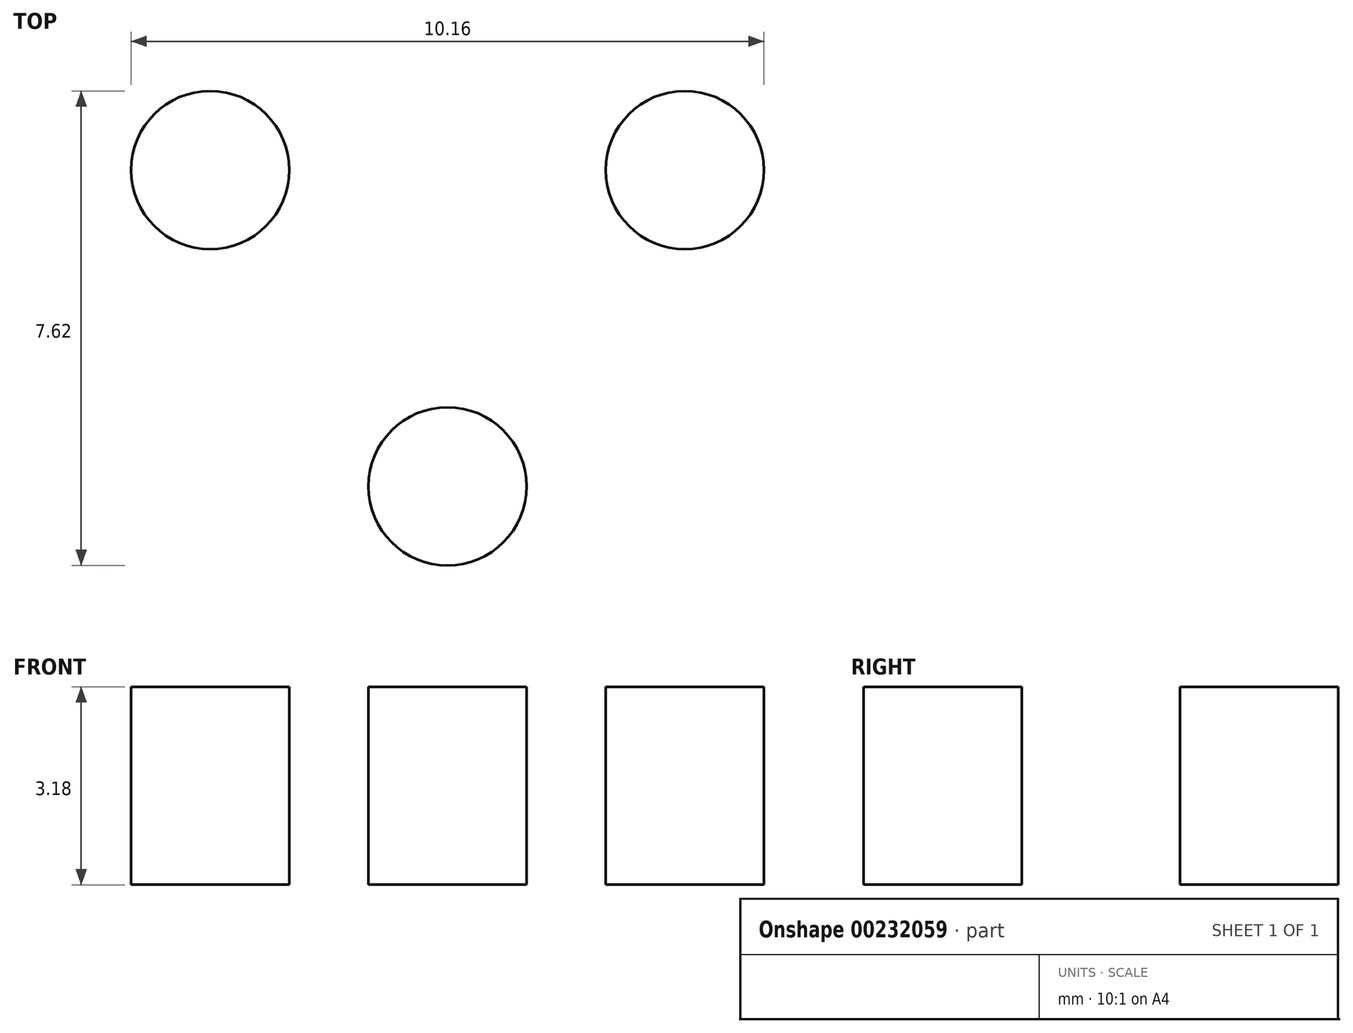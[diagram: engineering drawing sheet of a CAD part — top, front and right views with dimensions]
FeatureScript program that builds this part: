
annotation { "Feature Type Name" : "Feature", "Feature Type Description" : "" }
export const myFeature = defineFeature(function(context is Context, id is Id, definition is map)
    precondition{}
    {
        {
            var Q0;
            Q0=qCreatedBy(makeId("Top.planeOp"),FACE);
            var sketch = newSketch(context, id + "F0", { "sketchPlane" : qUnion([Q0])});
            skArc(sketch, "E0", {"start": v(0, 8.13) * mm, "mid": v(-8.13, 0) * mm, "end": v(0, -8.13) * mm});
            skLineSegment(sketch, "E1", {"start": v(0, 8.13) * mm, "end": v(20.32, 8.13) * mm});
            skLineSegment(sketch, "E2", {"start": v(0, -8.13) * mm, "end": v(18.29, -8.13) * mm});
            skArc(sketch, "E3", {"start": v(23.26, -9.18) * mm, "mid": v(18.82, -3.08) * mm, "end": v(13.2, -8.13) * mm});
            skLineSegment(sketch, "E4", {"start": v(20.32, 8.13) * mm, "end": v(37.22, -8.77) * mm});
            skLineSegment(sketch, "E5.0", {"start": v(23.26, -9.18) * mm, "end": v(31.82, -17.74) * mm});
            skPoint(sketch, "E6.centerSnap0", {"position": v(18.82, -3.08) * mm});
            skPoint(sketch, "E7.center.orphan", {"position": v(18.29, 8.13) * mm});
            skPoint(sketch, "E8.center.orphan", {"position": v(18.29, 0) * mm});
            skPoint(sketch, "E6.center.orphan", {"position": v(17.76, -3.08) * mm});
            skPoint(sketch, "E9.center.orphan", {"position": v(18.29, 2.23) * mm});
            skArc(sketch, "E10", {"start": v(31.82, -17.74) * mm, "mid": v(34.9, -13.49) * mm, "end": v(37.22, -8.77) * mm});
            skPoint(sketch, "E11.center.orphan", {"position": v(13.7, 2.23) * mm});
            skSolve(sketch);
        }
        {
            var Q0;
            {var subQ2=sQuery(id+"F0.wireOp",EDGE,"E0");Q0=makeQuery(id+"F0.imprint","IMPRINT",FACE,{"disambiguationData":[TD([[makeQuery(id+"F0.imprint","IMPRINT",EDGE,{"derivedFrom":subQ2}),1.0]])]});}
            extrude(context, id + "F1", {"entities" : qUnion([Q0]), "endBound" : BoundingType.SYMMETRIC, "depth" : 3.17 * mm});
        }
        {
            var Q0;
            Q0=makeQuery(id+"F1.opExtrude","CAP_FACE",FACE,{"disambiguationData":[OSD([sQuery(id+"F0.wireOp",EDGE,"E0"),sQuery(id+"F0.wireOp",EDGE,"E1"),sQuery(id+"F0.wireOp",EDGE,"E2"),sQuery(id+"F0.wireOp",EDGE,"E3"),sQuery(id+"F0.wireOp",EDGE,"E4"),sQuery(id+"F0.wireOp",EDGE,"E5.0"),sQuery(id+"F0.wireOp",EDGE,"E10")])],"isStart":false});
            var sketch = newSketch(context, id + "F2", { "sketchPlane" : qUnion([Q0])});
            skLineSegment(sketch, "E12", {"start": v(0, -8.13) * mm, "end": v(0, 8.13) * mm, "construction": true});
            skLineSegment(sketch, "E13.0", {"start": v(6.35, -8.13) * mm, "end": v(6.35, 8.13) * mm});
            skLineSegment(sketch, "E14.0", {"start": v(10.16, -8.13) * mm, "end": v(10.16, 8.13) * mm});
            skLineSegment(sketch, "E15.0", {"start": v(2.54, -8.13) * mm, "end": v(2.54, 8.13) * mm});
            skCircle(sketch, "E16", {"center": v(6.35, 5.08) * mm, "radius": 1.27 * mm});
            skCircle(sketch, "E17", {"center": v(6.35, -5.08) * mm, "radius": 1.27 * mm});
            skCircle(sketch, "E18", {"center": v(2.54, 0) * mm, "radius": 1.27 * mm});
            skCircle(sketch, "E19", {"center": v(10.16, 0) * mm, "radius": 1.27 * mm});
            skSolve(sketch);
        }
        {
            var Q0;
            {var subQ0=sQuery(id+"F2.wireOp",EDGE,"E19");var subQ1=sQuery(id+"F2.wireOp",EDGE,"E14.0");var subQ2=makeQuery(id+"F2.imprint","INTERSECT",VERTEX,{"disambiguationData":[OD(0.0)],"derivedFrom":[subQ1,subQ0]});Q0=makeQuery(id+"F2.imprint","IMPRINT",FACE,{"disambiguationData":[TD([[makeQuery(id+"F2.imprint","IMPRINT",EDGE,{"disambiguationData":[TD([[subQ2,-1.0]])],"derivedFrom":subQ1}),-1.0]])]});}
            var Q1;
            {var subQ0=sQuery(id+"F2.wireOp",EDGE,"E19");var subQ1=sQuery(id+"F2.wireOp",EDGE,"E14.0");var subQ2=makeQuery(id+"F2.imprint","INTERSECT",VERTEX,{"disambiguationData":[OD(0.0)],"derivedFrom":[subQ1,subQ0]});Q1=makeQuery(id+"F2.imprint","IMPRINT",FACE,{"disambiguationData":[TD([[makeQuery(id+"F2.imprint","IMPRINT",EDGE,{"disambiguationData":[TD([[subQ2,-1.0]])],"derivedFrom":subQ1}),1.0]])]});}
            var Q2;
            {var subQ0=sQuery(id+"F2.wireOp",EDGE,"E16");var subQ1=sQuery(id+"F2.wireOp",EDGE,"E13.0");var subQ2=makeQuery(id+"F2.imprint","INTERSECT",VERTEX,{"disambiguationData":[OD(0.0)],"derivedFrom":[subQ1,subQ0]});Q2=makeQuery(id+"F2.imprint","IMPRINT",FACE,{"disambiguationData":[TD([[makeQuery(id+"F2.imprint","IMPRINT",EDGE,{"disambiguationData":[TD([[subQ2,-1.0]])],"derivedFrom":subQ1}),-1.0]])]});}
            var Q3;
            {var subQ0=sQuery(id+"F2.wireOp",EDGE,"E16");var subQ1=sQuery(id+"F2.wireOp",EDGE,"E13.0");var subQ2=makeQuery(id+"F2.imprint","INTERSECT",VERTEX,{"disambiguationData":[OD(0.0)],"derivedFrom":[subQ1,subQ0]});Q3=makeQuery(id+"F2.imprint","IMPRINT",FACE,{"disambiguationData":[TD([[makeQuery(id+"F2.imprint","IMPRINT",EDGE,{"disambiguationData":[TD([[subQ2,-1.0]])],"derivedFrom":subQ1}),1.0]])]});}
            var Q4;
            {var subQ0=sQuery(id+"F2.wireOp",EDGE,"E18");var subQ1=sQuery(id+"F2.wireOp",EDGE,"E15.0");var subQ2=makeQuery(id+"F2.imprint","INTERSECT",VERTEX,{"disambiguationData":[OD(0.0)],"derivedFrom":[subQ1,subQ0]});Q4=makeQuery(id+"F2.imprint","IMPRINT",FACE,{"disambiguationData":[TD([[makeQuery(id+"F2.imprint","IMPRINT",EDGE,{"disambiguationData":[TD([[subQ2,-1.0]])],"derivedFrom":subQ1}),-1.0]])]});}
            var Q5;
            {var subQ0=sQuery(id+"F2.wireOp",EDGE,"E18");var subQ1=sQuery(id+"F2.wireOp",EDGE,"E15.0");var subQ2=makeQuery(id+"F2.imprint","INTERSECT",VERTEX,{"disambiguationData":[OD(0.0)],"derivedFrom":[subQ1,subQ0]});Q5=makeQuery(id+"F2.imprint","IMPRINT",FACE,{"disambiguationData":[TD([[makeQuery(id+"F2.imprint","IMPRINT",EDGE,{"disambiguationData":[TD([[subQ2,-1.0]])],"derivedFrom":subQ1}),1.0]])]});}
            var Q6;
            {var subQ0=sQuery(id+"F2.wireOp",EDGE,"E17");var subQ1=sQuery(id+"F2.wireOp",EDGE,"E13.0");var subQ2=makeQuery(id+"F2.imprint","INTERSECT",VERTEX,{"disambiguationData":[OD(0.0)],"derivedFrom":[subQ1,subQ0]});Q6=makeQuery(id+"F2.imprint","IMPRINT",FACE,{"disambiguationData":[TD([[makeQuery(id+"F2.imprint","IMPRINT",EDGE,{"disambiguationData":[TD([[subQ2,-1.0]])],"derivedFrom":subQ1}),1.0]])]});}
            var Q7;
            {var subQ0=sQuery(id+"F2.wireOp",EDGE,"E17");var subQ1=sQuery(id+"F2.wireOp",EDGE,"E13.0");var subQ2=makeQuery(id+"F2.imprint","INTERSECT",VERTEX,{"disambiguationData":[OD(0.0)],"derivedFrom":[subQ1,subQ0]});Q7=makeQuery(id+"F2.imprint","IMPRINT",FACE,{"disambiguationData":[TD([[makeQuery(id+"F2.imprint","IMPRINT",EDGE,{"disambiguationData":[TD([[subQ2,-1.0]])],"derivedFrom":subQ1}),-1.0]])]});}
            extrude(context, id + "F3", {"entities" : qUnion([Q0, Q1, Q2, Q3, Q4, Q5, Q6, Q7]), "operationType" : NewBodyOperationType.REMOVE, "oppositeDirection" : true, "depth" : 25.4 * mm});
        }
    });
